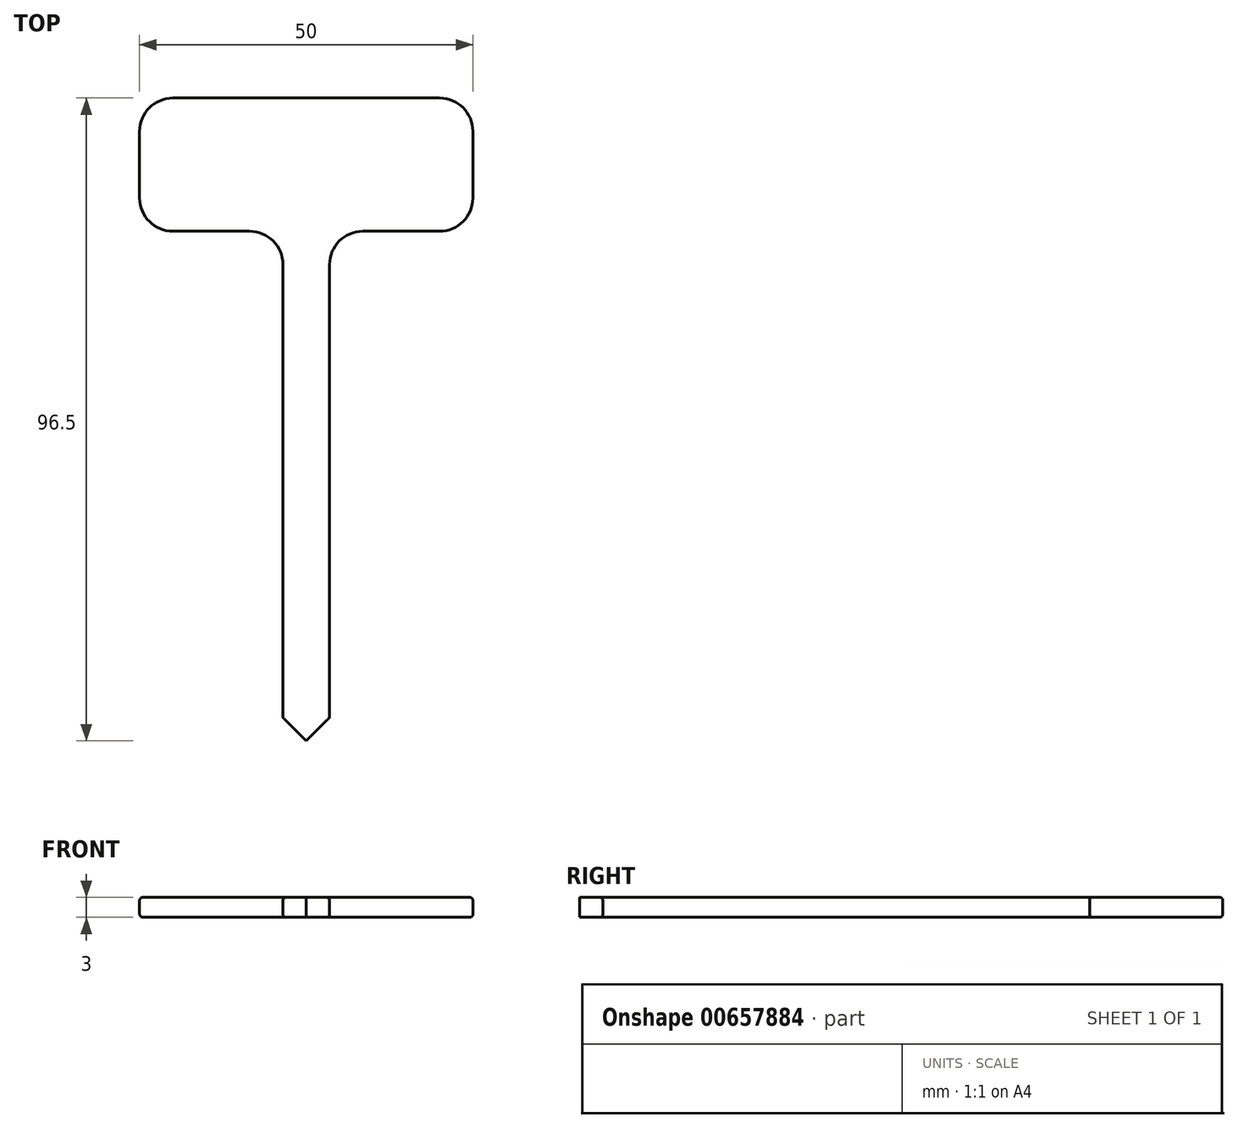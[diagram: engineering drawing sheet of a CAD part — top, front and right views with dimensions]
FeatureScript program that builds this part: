
annotation { "Feature Type Name" : "Feature", "Feature Type Description" : "" }
export const myFeature = defineFeature(function(context is Context, id is Id, definition is map)
    precondition{}
    {
        {
            var Q0;
            Q0=qCreatedBy(makeId("Top.planeOp"),FACE);
            var sketch = newSketch(context, id + "F0", { "sketchPlane" : qUnion([Q0])});
            skLineSegment(sketch, "E0.bottom", {"start": v(-25, 53.93) * mm, "end": v(25, 53.93) * mm});
            skLineSegment(sketch, "E0.top", {"start": v(-25, 73.93) * mm, "end": v(25, 73.93) * mm});
            skLineSegment(sketch, "E0.left", {"start": v(-25, 53.93) * mm, "end": v(-25, 73.93) * mm});
            skLineSegment(sketch, "E0.right", {"start": v(25, 53.93) * mm, "end": v(25, 73.93) * mm});
            skPoint(sketch, "E0.middle", {"position": v(0, 63.93) * mm});
            skLineSegment(sketch, "E1.bottom", {"start": v(3.5, 53.93) * mm, "end": v(-3.5, 53.93) * mm});
            skLineSegment(sketch, "E1.top", {"start": v(3.5, -26.07) * mm, "end": v(-3.5, -26.07) * mm});
            skLineSegment(sketch, "E1.left", {"start": v(3.5, 53.93) * mm, "end": v(3.5, -26.07) * mm});
            skLineSegment(sketch, "E1.right", {"start": v(-3.5, 53.93) * mm, "end": v(-3.5, -26.07) * mm});
            skLineSegment(sketch, "E2", {"start": v(0, -26.07) * mm, "end": v(0, -14.22) * mm, "construction": true});
            skSolve(sketch);
        }
        {
            var Q0;
            Q0 = qSketchRegion(id + "F0", true);
            extrude(context, id + "F1", {"entities" : qUnion([Q0]), "depth" : 3 * mm, "offsetDistance" : 25 * mm});
        }
        {
            var Q0;
            Q0=makeQuery(id+"F1.opExtrude","SWEPT_EDGE",EDGE,{"disambiguationData":[OSD([sQuery(id+"F0.wireOp",EDGE,"E0.top"),sQuery(id+"F0.wireOp",EDGE,"E0.left")])]});
            var Q1;
            Q1=makeQuery(id+"F1.opExtrude","SWEPT_EDGE",EDGE,{"disambiguationData":[OSD([sQuery(id+"F0.wireOp",EDGE,"E0.top"),sQuery(id+"F0.wireOp",EDGE,"E0.right")])]});
            var Q2;
            Q2=makeQuery(id+"F1.opExtrude","SWEPT_EDGE",EDGE,{"disambiguationData":[OSD([sQuery(id+"F0.wireOp",EDGE,"E0.bottom"),sQuery(id+"F0.wireOp",EDGE,"E0.right")])]});
            var Q3;
            Q3=makeQuery(id+"F1.opExtrude","SWEPT_EDGE",EDGE,{"disambiguationData":[OSD([sQuery(id+"F0.wireOp",EDGE,"E0.bottom"),sQuery(id+"F0.wireOp",EDGE,"E1.bottom"),sQuery(id+"F0.wireOp",EDGE,"E1.left")])]});
            var Q4;
            Q4=makeQuery(id+"F1.opExtrude","SWEPT_EDGE",EDGE,{"disambiguationData":[OSD([sQuery(id+"F0.wireOp",EDGE,"E0.bottom"),sQuery(id+"F0.wireOp",EDGE,"E1.bottom"),sQuery(id+"F0.wireOp",EDGE,"E1.right")])]});
            var Q5;
            Q5=makeQuery(id+"F1.opExtrude","SWEPT_EDGE",EDGE,{"disambiguationData":[OSD([sQuery(id+"F0.wireOp",EDGE,"E0.bottom"),sQuery(id+"F0.wireOp",EDGE,"E0.left")])]});
            fillet(context, id + "F2", {"entities" : qUnion([Q0, Q1, Q2, Q3, Q4, Q5]), "radius" : 5 * mm, "tangentPropagation" : true, "allowEdgeOverflow" : false});
        }
        {
            var Q0;
            Q0=makeQuery(id+"F1.opExtrude","SWEPT_EDGE",EDGE,{"disambiguationData":[OSD([sQuery(id+"F0.wireOp",EDGE,"E1.top"),sQuery(id+"F0.wireOp",EDGE,"E1.right")])]});
            var Q1;
            Q1=makeQuery(id+"F1.opExtrude","SWEPT_EDGE",EDGE,{"disambiguationData":[OSD([sQuery(id+"F0.wireOp",EDGE,"E1.top"),sQuery(id+"F0.wireOp",EDGE,"E1.left")])]});
            chamfer(context, id + "F3", {"entities" : qUnion([Q0, Q1]), "width" : 7 * mm, "tangentPropagation" : true});
        }
        {
            var Q0;
            Q0=makeQuery(id+"F1.opExtrude","CAP_EDGE",EDGE,{"disambiguationData":[OSD([sQuery(id+"F0.wireOp",EDGE,"E1.right")])],"isStart":false});
            var Q1;
            Q1=makeQuery(id+"F1.opExtrude","CAP_EDGE",EDGE,{"disambiguationData":[OSD([sQuery(id+"F0.wireOp",EDGE,"E1.right")])],"isStart":true});
            fillet(context, id + "F4", {"entities" : qUnion([Q0, Q1]), "radius" : 0.5 * mm, "tangentPropagation" : true, "allowEdgeOverflow" : false});
        }
    });
